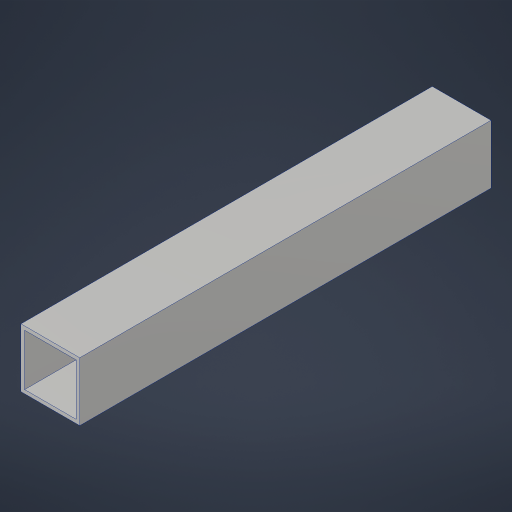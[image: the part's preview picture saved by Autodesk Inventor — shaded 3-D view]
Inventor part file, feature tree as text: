
AUTODESK INVENTOR PART (.ipt)
format: ipt  version: 2023.4 (Build 274418000, 418)  size: 164,352 bytes
history: native  units: in
note: dims shown in document units (in); Inventor stores cm internally (conversion verified against a paired STEP export)
features: extrude x1
ambient origin geometry x8: Origin, YZ Plane, XZ Plane, XY Plane, X Axis, Y Axis, Z Axis, Center Point
bodies: Solid1 (feature_tree)
feature tree (1):
  extrude  "Extrusion1"  TaperAngle=0.0deg  [1 undecoded]
note: 1 required parameter value undecoded (feature->parameter linkage not recoverable at this tier; creation-order binding heuristic only, values carry confidence <= 0.55)
